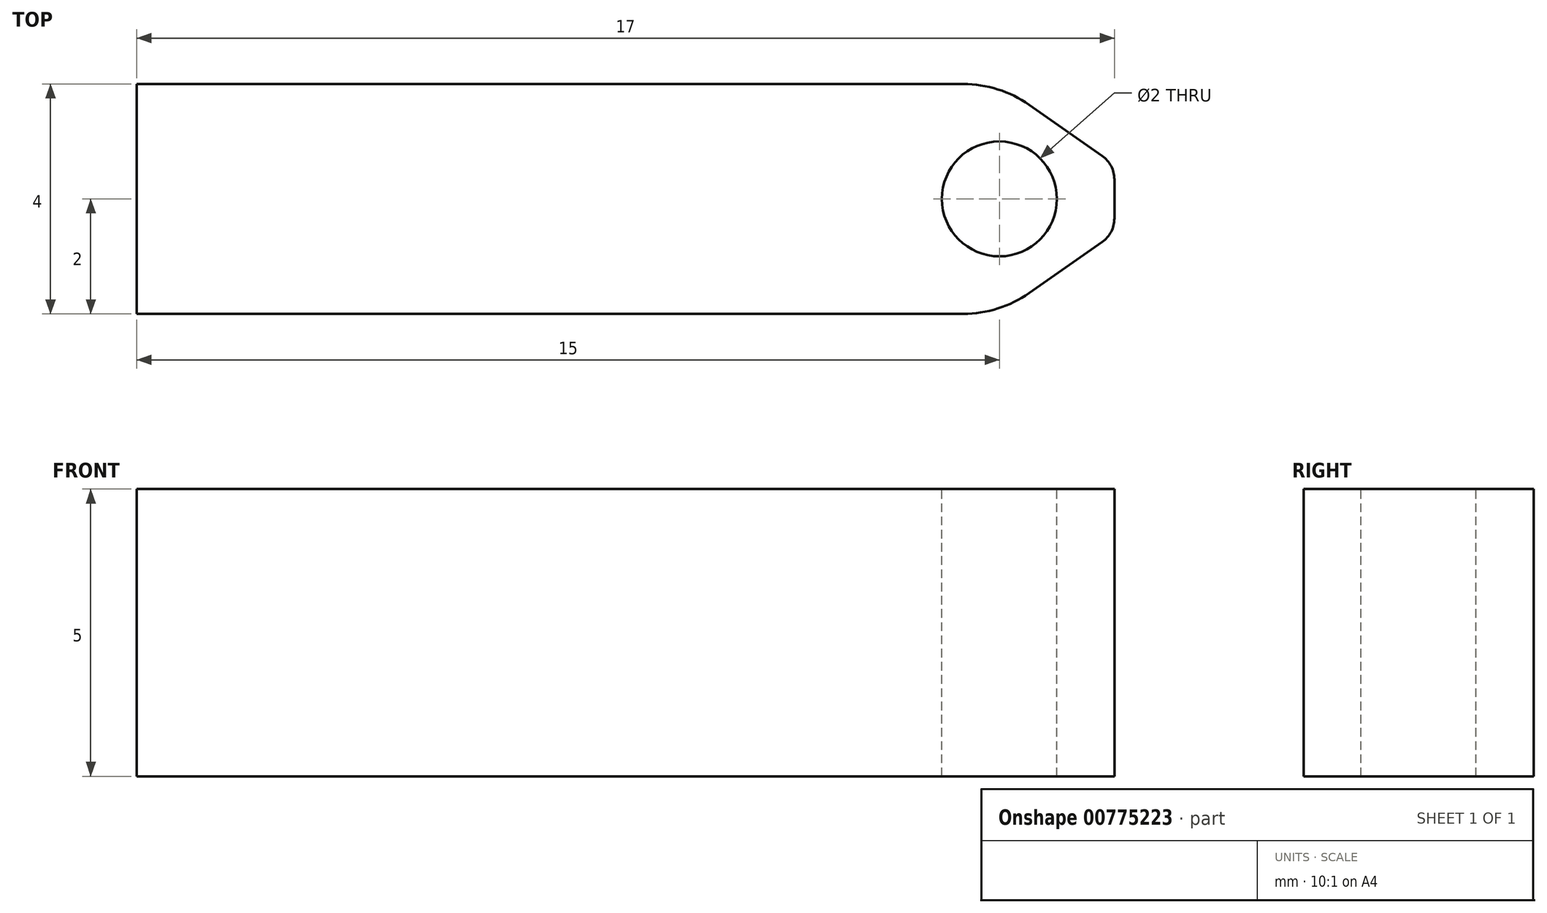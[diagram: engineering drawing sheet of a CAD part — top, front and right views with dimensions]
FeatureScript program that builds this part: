
annotation { "Feature Type Name" : "Feature", "Feature Type Description" : "" }
export const myFeature = defineFeature(function(context is Context, id is Id, definition is map)
    precondition{}
    {
        {
            var Q0;
            Q0=qCreatedBy(makeId("Top.planeOp"),FACE);
            var sketch = newSketch(context, id + "F0", { "sketchPlane" : qUnion([Q0])});
            skLineSegment(sketch, "E0.bottom", {"start": v(8.5, 2) * mm, "end": v(-8.5, 2) * mm});
            skLineSegment(sketch, "E0.top", {"start": v(8.5, -2) * mm, "end": v(-8.5, -2) * mm});
            skLineSegment(sketch, "E0.left", {"start": v(8.5, 2) * mm, "end": v(8.5, -2) * mm});
            skLineSegment(sketch, "E0.right", {"start": v(-8.5, 2) * mm, "end": v(-8.5, -2) * mm});
            skPoint(sketch, "E0.middle", {"position": v(0, 0) * mm});
            skSolve(sketch);
        }
        {
            var Q0;
            Q0 = qSketchRegion(id + "F0", true);
            extrude(context, id + "F1", {"entities" : qUnion([Q0]), "depth" : 5 * mm, "offsetDistance" : 25 * mm});
        }
        {
            var Q0;
            Q0=makeQuery(id+"F1.opExtrude","CAP_FACE",FACE,{"disambiguationData":[OSD([sQuery(id+"F0.wireOp",EDGE,"E0.bottom"),sQuery(id+"F0.wireOp",EDGE,"E0.top"),sQuery(id+"F0.wireOp",EDGE,"E0.left"),sQuery(id+"F0.wireOp",EDGE,"E0.right")])],"isStart":false});
            var sketch = newSketch(context, id + "F2", { "sketchPlane" : qUnion([Q0])});
            skPoint(sketch, "E1", {"position": v(6.5, 0) * mm});
            skSolve(sketch);
        }
        {
            var Q0;
            Q0=sQuery(id+"F2.wireOp",VERTEX,"E1");
            var Q1;
            Q1=makeQuery(id+"F1.opExtrude","SWEPT_BODY",BODY,{"disambiguationData":[OSD([sQuery(id+"F0.wireOp",EDGE,"E0.bottom"),sQuery(id+"F0.wireOp",EDGE,"E0.top"),sQuery(id+"F0.wireOp",EDGE,"E0.left"),sQuery(id+"F0.wireOp",EDGE,"E0.right")])]});
            hole(context, id + "F3", {"style" : HoleStyle.SIMPLE, "endStyle" : HoleEndStyle.THROUGH, "holeDiameter" : 2 * mm, "majorDiameter" : 5 * mm, "isTappedThrough" : true, "tappedDepth" : 12 * mm, "tapClearance" : 3, "locations" : qUnion([Q0]), "scope" : qUnion([Q1])});
        }
        {
            var Q0;
            Q0=makeQuery(id+"F1.opExtrude","SWEPT_EDGE",EDGE,{"disambiguationData":[OSD([sQuery(id+"F0.wireOp",EDGE,"E0.top"),sQuery(id+"F0.wireOp",EDGE,"E0.left")])]});
            var Q1;
            Q1=makeQuery(id+"F1.opExtrude","SWEPT_EDGE",EDGE,{"disambiguationData":[OSD([sQuery(id+"F0.wireOp",EDGE,"E0.bottom"),sQuery(id+"F0.wireOp",EDGE,"E0.left")])]});
            chamfer(context, id + "F4", {"entities" : qUnion([Q0, Q1]), "chamferType" : ChamferType.OFFSET_ANGLE, "width" : 1.4 * mm, "oppositeDirection" : false, "angle" : 55 * degree, "tangentPropagation" : true});
        }
        {
            var Q0;
            {var subQ0=sQuery(id+"F0.wireOp",EDGE,"E0.top");Q0=makeQuery(id+"F4.opChamfer","BLEND_EDGE",EDGE,{"blendedFrom":[makeQuery(id+"F1.opExtrude","SWEPT_EDGE",EDGE,{"disambiguationData":[OSD([subQ0,sQuery(id+"F0.wireOp",EDGE,"E0.left")])]}),makeQuery(id+"F1.opExtrude","SWEPT_FACE",FACE,{"disambiguationData":[OSD([subQ0])]})],"blendedInto":[makeQuery(id+"F1.opExtrude","SWEPT_FACE",FACE,{"disambiguationData":[OSD([subQ0])]})]});}
            var Q1;
            {var subQ0=sQuery(id+"F0.wireOp",EDGE,"E0.bottom");Q1=makeQuery(id+"F4.opChamfer","BLEND_EDGE",EDGE,{"blendedFrom":[makeQuery(id+"F1.opExtrude","SWEPT_EDGE",EDGE,{"disambiguationData":[OSD([subQ0,sQuery(id+"F0.wireOp",EDGE,"E0.left")])]}),makeQuery(id+"F1.opExtrude","SWEPT_FACE",FACE,{"disambiguationData":[OSD([subQ0])]})],"blendedInto":[makeQuery(id+"F1.opExtrude","SWEPT_FACE",FACE,{"disambiguationData":[OSD([subQ0])]})]});}
            fillet(context, id + "F5", {"entities" : qUnion([Q0, Q1]), "radius" : 2 * mm, "tangentPropagation" : true, "allowEdgeOverflow" : false});
        }
        {
            var Q0;
            {var subQ0=sQuery(id+"F0.wireOp",EDGE,"E0.left");Q0=makeQuery(id+"F4.opChamfer","BLEND_EDGE",EDGE,{"blendedFrom":[makeQuery(id+"F1.opExtrude","SWEPT_EDGE",EDGE,{"disambiguationData":[OSD([sQuery(id+"F0.wireOp",EDGE,"E0.bottom"),subQ0])]}),makeQuery(id+"F1.opExtrude","SWEPT_FACE",FACE,{"disambiguationData":[OSD([subQ0])]})],"blendedInto":[makeQuery(id+"F1.opExtrude","SWEPT_FACE",FACE,{"disambiguationData":[OSD([subQ0])]})]});}
            var Q1;
            {var subQ0=sQuery(id+"F0.wireOp",EDGE,"E0.left");Q1=makeQuery(id+"F4.opChamfer","BLEND_EDGE",EDGE,{"blendedFrom":[makeQuery(id+"F1.opExtrude","SWEPT_EDGE",EDGE,{"disambiguationData":[OSD([sQuery(id+"F0.wireOp",EDGE,"E0.top"),subQ0])]}),makeQuery(id+"F1.opExtrude","SWEPT_FACE",FACE,{"disambiguationData":[OSD([subQ0])]})],"blendedInto":[makeQuery(id+"F1.opExtrude","SWEPT_FACE",FACE,{"disambiguationData":[OSD([subQ0])]})]});}
            fillet(context, id + "F6", {"entities" : qUnion([Q0, Q1]), "radius" : 0.5 * mm, "tangentPropagation" : true, "allowEdgeOverflow" : false});
        }
    });
